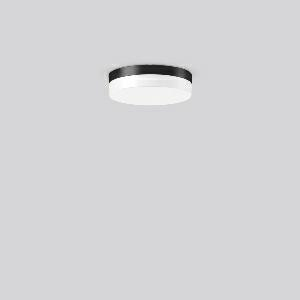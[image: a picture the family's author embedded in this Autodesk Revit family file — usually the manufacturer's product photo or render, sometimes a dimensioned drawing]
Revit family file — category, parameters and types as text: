
# Revit family: flat_slim_round_312135_0031_1_19_4d22
name_source: partatom
category: Lighting Fixtures
units: mm (PartAtom-declared; Revit-internal decimal feet)

## family parameters
Cut with Voids When Loaded = No
Host = Face
Light Source = No
Part Type = Normal
Room Calculation Point = No
Round Connector Dimension = Use Diameter
Shared = No

## types (1)
- FLAT SLIM round (1 x LED Modul 840, 1100 lm, 4000)
    Apparent Load = 12 VA
    CIE Flux Codes = 43 74 92 91 100
    Color Rendering = 80
    Color Temperature = 4000
    Default Elevation = 1800 mm
    Height = 63 mm
    Lamp = 1 x LED Modul 840
    Lamp Light Flux = 1100 lm
    Lamp count = 1
    Length = 230 mm
    Lifetime = 50000 h
    Luminous efficacy = 92 lm/W
    Manufacturer = RZB
    ModVariant = No
    Model = 312135.0031.1.19
    Mounting Place = Ceiling, Wall
    Mounting Type = Surface mounted
    Number of Poles = 1
    OnlyDefault = Yes
    Power Factor = 1
    Product Name = FLAT SLIM round
    Product group = Surface mounted ceiling and wall luminaires
    ProductGroupID = 305
    Protection Class = Protection class I
    Protection Degree = IP 65
    RLX_Detail_Level = 1
    RLX_Emergency_Light_Flux = 0 lm
    RLX_Emergency_Type = 0
    RLX_Emergency_Type_DB = No
    RlxData = <blob elided: 18465 chars, md5=30f483f4>
    Socket = socket
    Standby Power = 0 W
    System Light Flux = 1100 lm
    System Power = 12 W
    Type Comments = Product without accessories
    Type Image = 312132.0031.jpg
    URL = http://relux.com
    VarID = ---
    Voltage = 230 V
    Voltage Range = 220-240 V
    Weight = 0.00 kg
    Width = 0 mm  [stored 0 ft]

note: [stored X ft] marks values corroborated as IEEE doubles in the binary element streams (Revit-internal decimal feet)

## geometry (parser evidence)
native form markers: Blend x4, Sweep x14
no freeform markers — native parametric forms only
